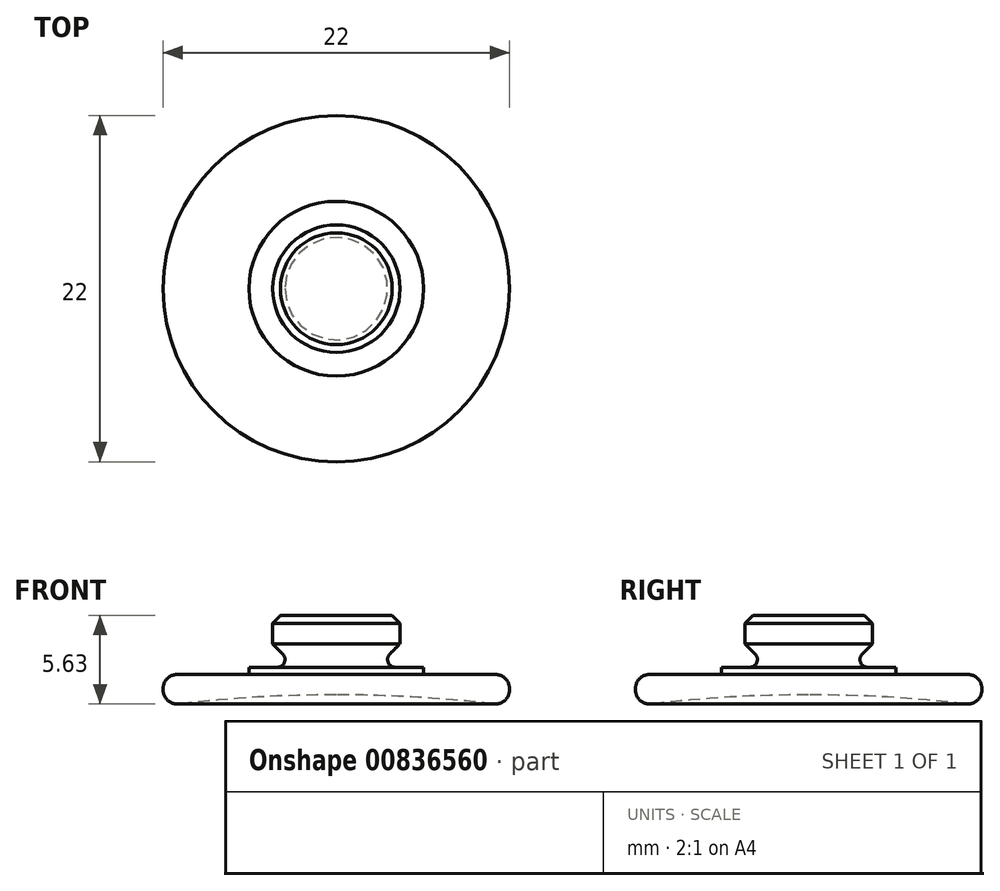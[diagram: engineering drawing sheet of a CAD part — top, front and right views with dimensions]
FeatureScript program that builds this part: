
annotation { "Feature Type Name" : "Feature", "Feature Type Description" : "" }
export const myFeature = defineFeature(function(context is Context, id is Id, definition is map)
    precondition{}
    {
        {
            var Q0;
            Q0=qCreatedBy(makeId("Front.planeOp"),FACE);
            var sketch = newSketch(context, id + "F0", { "sketchPlane" : qUnion([Q0])});
            skLineSegment(sketch, "E0", {"start": v(0, 0) * mm, "end": v(11, 0) * mm, "construction": true});
            skLineSegment(sketch, "E1", {"start": v(11, 0) * mm, "end": v(11, 2) * mm});
            skLineSegment(sketch, "E2", {"start": v(11, 2) * mm, "end": v(5.55, 2) * mm});
            skLineSegment(sketch, "E3", {"start": v(5.55, 2) * mm, "end": v(5.55, 2.45) * mm});
            skLineSegment(sketch, "E4", {"start": v(4.05, 3.95) * mm, "end": v(4.05, 5.75) * mm});
            skLineSegment(sketch, "E5", {"start": v(4.05, 5.75) * mm, "end": v(0, 5.75) * mm});
            skLineSegment(sketch, "E6", {"start": v(0, 5.75) * mm, "end": v(0, 0.7) * mm});
            skLineSegment(sketch, "E7", {"start": v(5.55, 2.45) * mm, "end": v(2.55, 2.45) * mm});
            skPoint(sketch, "E8.orphan", {"position": v(2.55, 1.8) * mm});
            skLineSegment(sketch, "E9", {"start": v(2.55, 2.45) * mm, "end": v(4.05, 3.95) * mm});
            skPoint(sketch, "E10.end.orphan", {"position": v(2.55, 3.1) * mm});
            skArc(sketch, "E11", {"start": v(11, 0) * mm, "mid": v(5.51, 0.52) * mm, "end": v(0, 0.7) * mm});
            skSolve(sketch);
        }
        {
            var Q0;
            Q0=makeQuery(id+"F0.imprint","IMPRINT",FACE,{"disambiguationData":[TD([[makeQuery(id+"F0.imprint","IMPRINT",EDGE,{"derivedFrom":sQuery(id+"F0.wireOp",EDGE,"E1")}),1.0]])]});
            var Q1;
            Q1=sQuery(id+"F0.wireOp",EDGE,"E6");
            revolve(context, id + "F1", {"surfaceOperationType" : NewSurfaceOperationType.NEW, "entities" : qUnion([Q0]), "axis" : qUnion([Q1]), "revolveType" : RevolveType.FULL});
        }
        {
            var Q0;
            Q0=makeQuery(id+"F1.opRevolve","SWEPT_EDGE",EDGE,{"disambiguationData":[OSD([sQuery(id+"F0.wireOp",EDGE,"E7"),sQuery(id+"F0.wireOp",EDGE,"E9")])]});
            fillet(context, id + "F2", {"entities" : qUnion([Q0]), "radius" : 0.5 * mm, "tangentPropagation" : true, "allowEdgeOverflow" : false});
        }
        {
            var Q0;
            Q0=makeQuery(id+"F1.opRevolve","SWEPT_EDGE",EDGE,{"disambiguationData":[OSD([sQuery(id+"F0.wireOp",EDGE,"E0"),sQuery(id+"F0.wireOp",EDGE,"E1")])]});
            var Q1;
            Q1=makeQuery(id+"F1.opRevolve","SWEPT_EDGE",EDGE,{"disambiguationData":[OSD([sQuery(id+"F0.wireOp",EDGE,"E1"),sQuery(id+"F0.wireOp",EDGE,"E2")])]});
            fillet(context, id + "F3", {"entities" : qUnion([Q0, Q1]), "radius" : 0.9 * mm, "tangentPropagation" : true, "allowEdgeOverflow" : false});
        }
        {
            var Q0;
            Q0=makeQuery(id+"F1.opRevolve","SWEPT_FACE",FACE,{"disambiguationData":[OSD([sQuery(id+"F0.wireOp",EDGE,"E5")])]});
            chamfer(context, id + "F4", {"entities" : qUnion([Q0]), "width" : 0.5 * mm, "tangentPropagation" : true});
        }
    });
